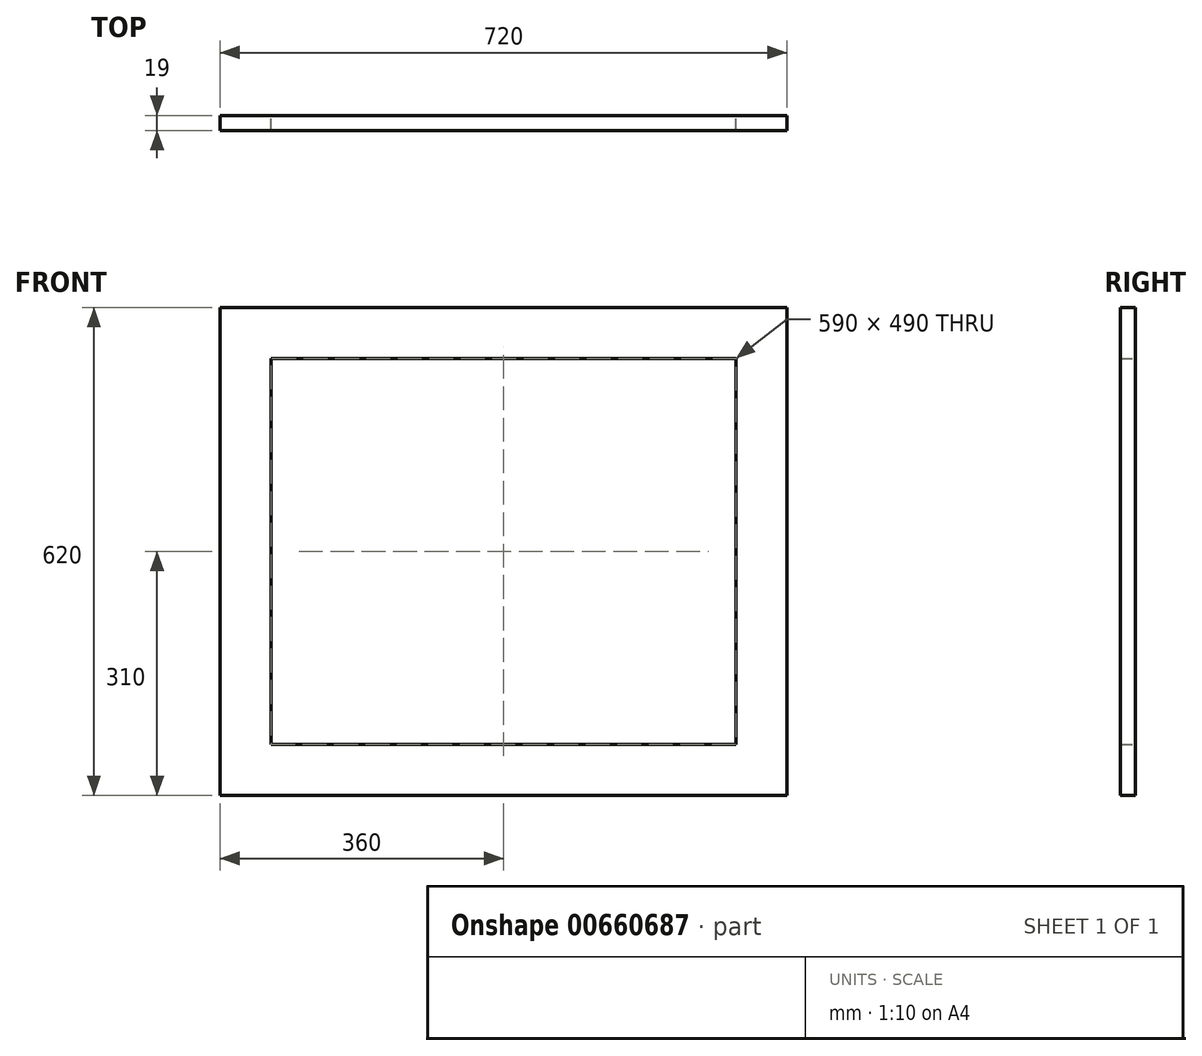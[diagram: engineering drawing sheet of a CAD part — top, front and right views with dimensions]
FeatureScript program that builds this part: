
annotation { "Feature Type Name" : "Feature", "Feature Type Description" : "" }
export const myFeature = defineFeature(function(context is Context, id is Id, definition is map)
    precondition{}
    {
        {
            var Q0;
            Q0=qCreatedBy(makeId("Front.planeOp"),FACE);
            var sketch = newSketch(context, id + "F0", { "sketchPlane" : qUnion([Q0])});
            skLineSegment(sketch, "E0.bottom", {"start": v(0, 0) * mm, "end": v(590, 0) * mm});
            skLineSegment(sketch, "E0.top", {"start": v(0, 490) * mm, "end": v(590, 490) * mm});
            skLineSegment(sketch, "E0.left", {"start": v(0, 0) * mm, "end": v(0, 490) * mm});
            skLineSegment(sketch, "E0.right", {"start": v(590, 0) * mm, "end": v(590, 490) * mm});
            skLineSegment(sketch, "E1.0", {"start": v(655, -65) * mm, "end": v(655, 555) * mm});
            skLineSegment(sketch, "E1.1", {"start": v(-65, -65) * mm, "end": v(655, -65) * mm});
            skLineSegment(sketch, "E1.2", {"start": v(-65, -65) * mm, "end": v(-65, 555) * mm});
            skLineSegment(sketch, "E1.3", {"start": v(-65, 555) * mm, "end": v(655, 555) * mm});
            skSolve(sketch);
        }
        {
            var Q0;
            Q0=qSketchRegion(id+"F0",true);
            extrude(context, id + "F1", {"entities" : qUnion([Q0]), "depth" : 19 * mm, "offsetDistance" : 25 * mm});
        }
    });
